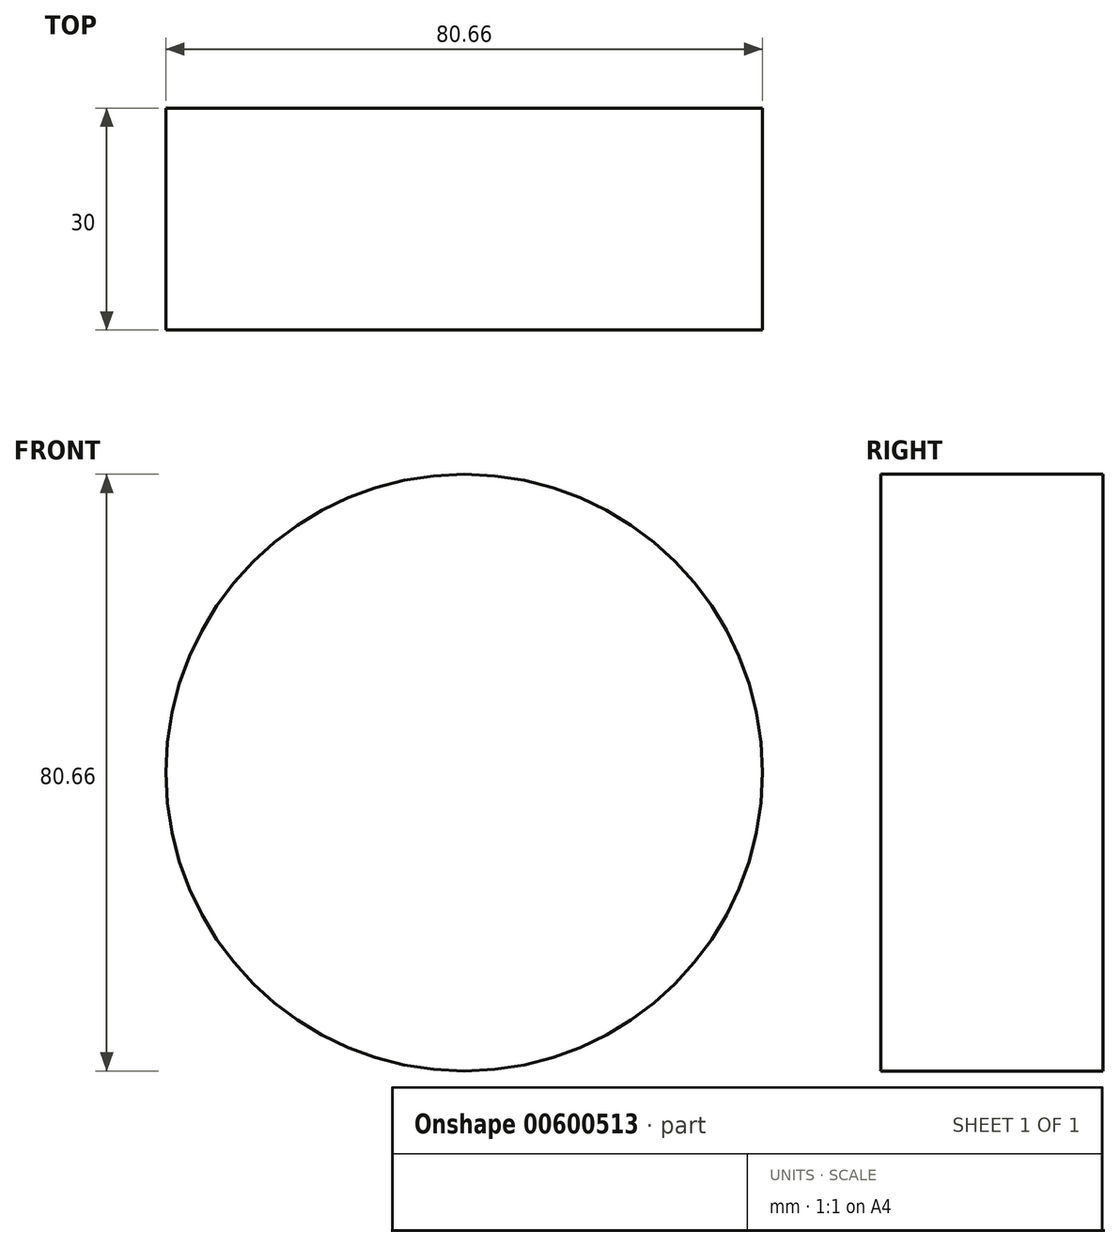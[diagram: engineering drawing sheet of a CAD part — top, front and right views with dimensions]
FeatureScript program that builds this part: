
annotation { "Feature Type Name" : "Feature", "Feature Type Description" : "" }
export const myFeature = defineFeature(function(context is Context, id is Id, definition is map)
    precondition{}
    {
        {
            var Q0;
            Q0=qCreatedBy(makeId("Front.planeOp"),FACE);
            var sketch = newSketch(context, id + "F0", { "sketchPlane" : qUnion([Q0])});
            skCircle(sketch, "E0", {"center": v(0, 0) * mm, "radius": 40.33 * mm});
            skSolve(sketch);
        }
        {
            var Q0;
            Q0=sQuery(id+"F0.wireOp",EDGE,"E0");
            extrude(context, id + "F1", {"bodyType" : ToolBodyType.SURFACE, "surfaceEntities" : qUnion([Q0]), "depth" : 30 * mm, "offsetDistance" : 25 * mm});
        }
    });
